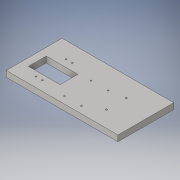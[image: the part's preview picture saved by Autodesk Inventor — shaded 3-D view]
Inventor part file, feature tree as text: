
AUTODESK INVENTOR PART (.ipt)
format: ipt  version: 2016 (Build 200138000, 138)  size: 160,256 bytes
history: native  units: in
note: dims shown in document units (in); Inventor stores cm internally (conversion verified against a paired STEP export)
features: extrude x5, sketch x5
ambient origin geometry x8: Origin, YZ Plane, XZ Plane, XY Plane, X Axis, Y Axis, Z Axis, Center Point
bodies: Solid1 (feature_tree)
feature tree (10):
  extrude  "RectangleFace"  Depth=5.5512in
  extrude  "RectangularCut"  Depth=0.5906in
  extrude  "AxleSupportHoles"  Depth=3.1496in
  extrude  "DriverHoles"  Depth=0.5906in TaperAngle=0.0deg
  extrude  "Extrusion5"  Depth=0.5906in
  sketch  "Sketch1"  dims[d0=11.1024in d1=5.5512in]
  sketch  "Sketch2"  dims[d2=0.5906in d3=0.0in d4=3.2126in]
  sketch  "Sketch3"  dims[d5=3.2283in d6=3.1496in]
  sketch  "Sketch4"  dims[d7=1.7717in d8=0.5906in d9=0.0in]
  sketch  "Sketch5"  dims[d10=0.7087in d11=0.4921in d12=0.315in d13=0.315in d14=0.315in d15=0.315in d16=0.1378in d17=0.1378in d18=0.1378in d19=0.1378in d20=0.5906in d21=0.0in d22=3.5433in d23=0.3937in d24=2.0079in d25=2.9724in d26=0.1575in d27=0.1575in d28=0.1575in d29=0.1575in d30=0.1575in d31=0.1575in d32=0.1575in d33=0.1575in d34=0.1378in d35=0.1378in d36=0.1378in d37=0.1378in d38=0.5906in d39=0.0in d40=2.7559in d41=1.9685in d42=90.0deg d43=1.9685in d44=180.0deg d45=0.1575in d46=0.1575in d47=0.5906in d48=0.0in]
